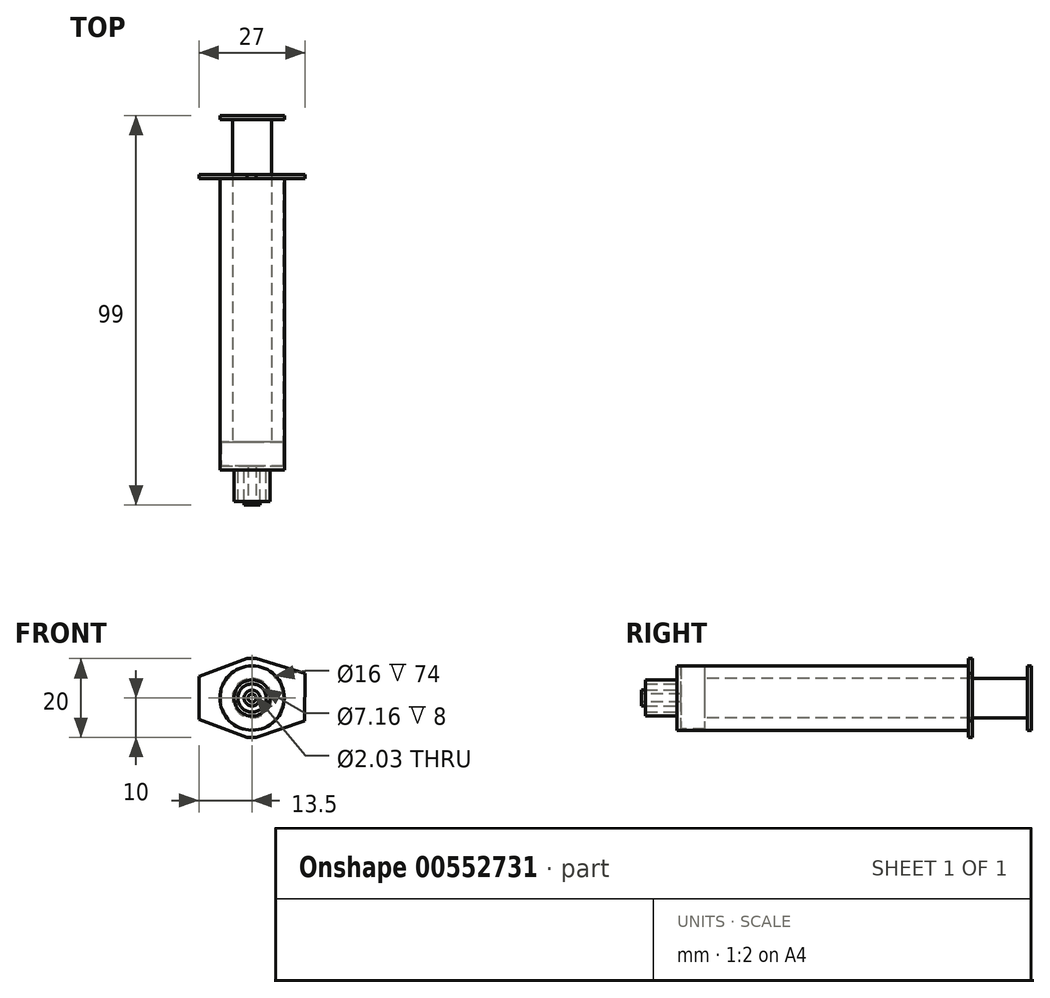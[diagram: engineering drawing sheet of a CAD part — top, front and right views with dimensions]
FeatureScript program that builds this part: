
annotation { "Feature Type Name" : "Feature", "Feature Type Description" : "" }
export const myFeature = defineFeature(function(context is Context, id is Id, definition is map)
    precondition{}
    {
        {
            var Q0;
            Q0=qCreatedBy(makeId("Front.planeOp"),FACE);
            var sketch = newSketch(context, id + "F0", { "sketchPlane" : qUnion([Q0])});
            skCircle(sketch, "E0", {"center": v(0, 0) * mm, "radius": 8.2 * mm});
            skSolve(sketch);
        }
        {
            var Q0;
            Q0=makeQuery(id+"F0.imprint","IMPRINT",FACE,{"disambiguationData":[TD([[makeQuery(id+"F0.imprint","IMPRINT",EDGE,{"derivedFrom":sQuery(id+"F0.wireOp",EDGE,"E0")}),1.0]])]});
            extrude(context, id + "F1", {"entities" : qUnion([Q0]), "depth" : 75 * mm, "offsetDistance" : 25 * mm});
        }
        {
            var Q0;
            Q0=qCreatedBy(makeId("Front.planeOp"),FACE);
            var sketch = newSketch(context, id + "F2", { "sketchPlane" : qUnion([Q0])});
            skPoint(sketch, "E1.middle", {"position": v(0, 0) * mm});
            skLineSegment(sketch, "E2", {"start": v(-13.5, 5.43) * mm, "end": v(-1.33, 10) * mm});
            skLineSegment(sketch, "E3", {"start": v(-1.33, 10) * mm, "end": v(1.06, 10) * mm});
            skLineSegment(sketch, "E4", {"start": v(1.06, 10) * mm, "end": v(13.5, 6.21) * mm});
            skLineSegment(sketch, "E5", {"start": v(-13.5, -5.43) * mm, "end": v(-1.33, -10) * mm});
            skLineSegment(sketch, "E6", {"start": v(-1.33, -10) * mm, "end": v(1.06, -10) * mm});
            skLineSegment(sketch, "E7", {"start": v(1.06, -10) * mm, "end": v(13.36, -5.79) * mm});
            skLineSegment(sketch, "E8", {"start": v(13.5, 6.21) * mm, "end": v(13.36, -5.79) * mm});
            skLineSegment(sketch, "E9", {"start": v(-13.5, 5.43) * mm, "end": v(-13.5, -5.43) * mm});
            skCircle(sketch, "E10", {"center": v(0, 0) * mm, "radius": 7.5 * mm});
            skSolve(sketch);
        }
        {
            var Q0;
            Q0=makeQuery(id+"F2.imprint","IMPRINT",FACE,{"disambiguationData":[TD([[makeQuery(id+"F2.imprint","IMPRINT",EDGE,{"derivedFrom":sQuery(id+"F2.wireOp",EDGE,"E2")}),-1.0]])]});
            extrude(context, id + "F3", {"entities" : qUnion([Q0]), "operationType" : NewBodyOperationType.ADD, "depth" : 1 * mm, "offsetDistance" : 25 * mm});
        }
        {
            var Q0;
            Q0=qCreatedBy(makeId("Front.planeOp"),FACE);
            var sketch = newSketch(context, id + "F4", { "sketchPlane" : qUnion([Q0])});
            skCircle(sketch, "E11", {"center": v(0, 0) * mm, "radius": 8 * mm});
            skSolve(sketch);
        }
        {
            var Q0;
            Q0=makeQuery(id+"F4.imprint","IMPRINT",FACE,{"disambiguationData":[TD([[makeQuery(id+"F4.imprint","IMPRINT",EDGE,{"derivedFrom":sQuery(id+"F4.wireOp",EDGE,"E11")}),1.0]])]});
            extrude(context, id + "F5", {"entities" : qUnion([Q0]), "operationType" : NewBodyOperationType.REMOVE, "depth" : 74 * mm, "offsetDistance" : 25 * mm});
        }
        {
            var Q0;
            Q0=makeQuery(id+"F1.opExtrude","CAP_FACE",FACE,{"disambiguationData":[OSD([sQuery(id+"F0.wireOp",EDGE,"E0")])],"isStart":false});
            var sketch = newSketch(context, id + "F6", { "sketchPlane" : qUnion([Q0])});
            skCircle(sketch, "E12", {"center": v(0, 0) * mm, "radius": 4.58 * mm});
            skCircle(sketch, "E13", {"center": v(0, 0) * mm, "radius": 3.58 * mm});
            skSolve(sketch);
        }
        {
            var Q0;
            Q0=makeQuery(id+"F6.imprint","IMPRINT",FACE,{"disambiguationData":[TD([[makeQuery(id+"F6.imprint","IMPRINT",EDGE,{"derivedFrom":sQuery(id+"F6.wireOp",EDGE,"E12")}),1.0]])]});
            extrude(context, id + "F7", {"entities" : qUnion([Q0]), "operationType" : NewBodyOperationType.ADD, "depth" : 8 * mm, "offsetDistance" : 25 * mm});
        }
        {
            var Q0;
            Q0=makeQuery(id+"F7.boolean.opBoolean","SPLIT",FACE,{"disambiguationData":[TD([makeQuery(id+"F7.opExtrude","SWEPT_FACE",FACE,{"disambiguationData":[OSD([sQuery(id+"F6.wireOp",EDGE,"E13")])]})])],"derivedFrom":makeQuery(id+"F1.opExtrude","CAP_FACE",FACE,{"disambiguationData":[OSD([sQuery(id+"F0.wireOp",EDGE,"E0")])],"isStart":false})});
            var sketch = newSketch(context, id + "F8", { "sketchPlane" : qUnion([Q0])});
            skCircle(sketch, "E14", {"center": v(0, 0) * mm, "radius": 2.02 * mm});
            skSolve(sketch);
        }
        {
            var Q0;
            Q0=qSketchRegion(id+"F8",true);
            extrude(context, id + "F9", {"entities" : qUnion([Q0]), "operationType" : NewBodyOperationType.ADD, "depth" : 9 * mm, "offsetDistance" : 25 * mm});
        }
        {
            var Q0;
            Q0=makeQuery(id+"F9.opExtrude","CAP_FACE",FACE,{"disambiguationData":[OSD([sQuery(id+"F8.wireOp",EDGE,"E14")])],"isStart":false});
            var sketch = newSketch(context, id + "F10", { "sketchPlane" : qUnion([Q0])});
            skCircle(sketch, "E15", {"center": v(0, 0) * mm, "radius": 1.01 * mm});
            skSolve(sketch);
        }
        {
            var Q0;
            Q0=qSketchRegion(id+"F10",true);
            extrude(context, id + "F11", {"entities" : qUnion([Q0]), "operationType" : NewBodyOperationType.REMOVE, "oppositeDirection" : true, "depth" : 75 * mm, "offsetDistance" : 25 * mm});
        }
        {
            var Q0;
            Q0=makeQuery(id+"F5.boolean.opBoolean","COPY",FACE,{"derivedFrom":makeQuery(id+"F5.opExtrude","CAP_FACE",FACE,{"disambiguationData":[OSD([sQuery(id+"F4.wireOp",EDGE,"E11")])],"isStart":false})});
            var sketch = newSketch(context, id + "F12", { "sketchPlane" : qUnion([Q0])});
            skCircle(sketch, "E16", {"center": v(0, 0) * mm, "radius": 7.9 * mm});
            skSolve(sketch);
        }
        {
            var Q0;
            Q0=qSketchRegion(id+"F12",true);
            extrude(context, id + "F13", {"entities" : qUnion([Q0]), "depth" : 6 * mm, "offsetDistance" : 25 * mm});
        }
        {
            var Q0;
            Q0=makeQuery(id+"F13.opExtrude","CAP_FACE",FACE,{"disambiguationData":[OSD([sQuery(id+"F12.wireOp",EDGE,"E16")])],"isStart":false});
            var sketch = newSketch(context, id + "F14", { "sketchPlane" : qUnion([Q0])});
            skCircle(sketch, "E17", {"center": v(0, 0) * mm, "radius": 5 * mm});
            skSolve(sketch);
        }
        {
            var Q0;
            Q0=qSketchRegion(id+"F14",true);
            extrude(context, id + "F15", {"entities" : qUnion([Q0]), "operationType" : NewBodyOperationType.ADD, "depth" : 82 * mm, "offsetDistance" : 25 * mm});
        }
        {
            var Q0;
            Q0=makeQuery(id+"F15.opExtrude","CAP_FACE",FACE,{"disambiguationData":[OSD([sQuery(id+"F14.wireOp",EDGE,"E17")])],"isStart":false});
            var sketch = newSketch(context, id + "F16", { "sketchPlane" : qUnion([Q0])});
            skCircle(sketch, "E18", {"center": v(0, 0) * mm, "radius": 8.2 * mm});
            skSolve(sketch);
        }
        {
            var Q0;
            Q0=qSketchRegion(id+"F16",true);
            extrude(context, id + "F17", {"entities" : qUnion([Q0]), "operationType" : NewBodyOperationType.ADD, "depth" : 1 * mm, "offsetDistance" : 25 * mm});
        }
    });
